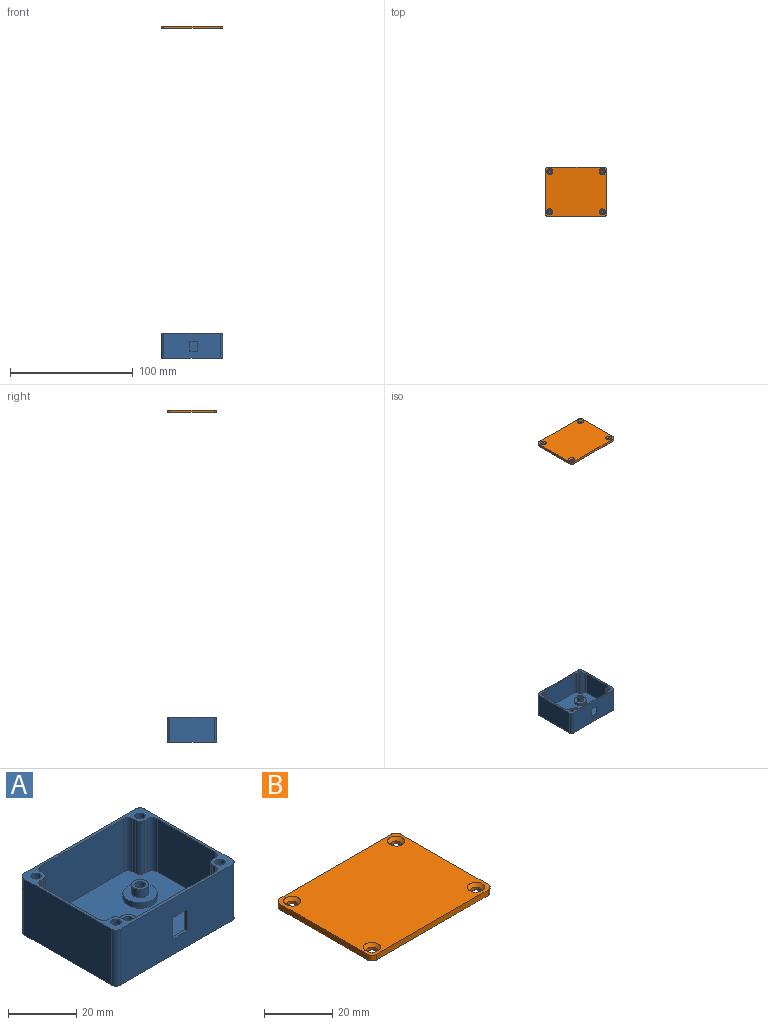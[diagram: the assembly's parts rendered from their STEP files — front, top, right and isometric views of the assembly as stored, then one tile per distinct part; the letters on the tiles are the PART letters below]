
ASSEMBLY  parts=2 mates=1
PART A: 71 faces, bbox 50x40x20 mm
  f0: plane 34x19mm, normal (0,1,0), area 598.7mm2, adj f4,f8,f51,f55,f67,f68,f69,f70
  f1: plane 46x20mm, normal (0,-1,0), area 872.7mm2, adj f8,f12,f64,f65,f67,f68,f69,f70
  f2: cylinder r=1.5mm len=4mm, axis (0,0,-1), area 37.7mm2, adj f30,f50
  f3: cylinder r=1.5mm len=4mm, axis (0,0,-1), area 37.7mm2, adj f32,f43
  f4: plane 48x38mm, normal (0,0,1), area 1563.5mm2, adj f0,f5,f6,f7,f13,f14,f15,f16
  f5: plane 24x19mm, normal (-1,0,0), area 456mm2, adj f4,f8,f53,f57
  f6: plane 34x19mm, normal (0,-1,0), area 646mm2, adj f4,f8,f58,f60
  f7: plane 24x19mm, normal (1,0,0), area 456mm2, adj f4,f8,f56,f62
  f8: plane 50x40mm, normal (0,0,1), area 247.7mm2, adj f0,f1,f5,f6,f7,f9,f10,f11
  f9: plane 46x20mm, normal (0,1,0), area 920mm2, adj f8,f12,f63,f66
  f10: plane 36x20mm, normal (-1,0,0), area 720mm2, adj f8,f12,f63,f64
  f11: plane 36x20mm, normal (1,0,0), area 720mm2, adj f8,f12,f65,f66
  f12: plane 50x40mm, normal (0,0,-1), area 1949.8mm2, adj f1,f9,f10,f11,f37,f38,f39,f40
  f13: plane 19x1mm, normal (0,-1,0), area 19mm2, adj f4,f8,f61,f62
  f14: plane 19x1mm, normal (1,0,0), area 19mm2, adj f4,f8,f60,f61
  f15: plane 19x1mm, normal (0,-1,0), area 19mm2, adj f4,f8,f57,f59
  f16: plane 19x1mm, normal (-1,0,0), area 19mm2, adj f4,f8,f58,f59
  f17: plane 19x1mm, normal (0,1,0), area 19mm2, adj f4,f8,f52,f53
  f18: plane 19x1mm, normal (-1,0,0), area 19mm2, adj f4,f8,f51,f52
  f19: plane 19x1mm, normal (0,1,0), area 19mm2, adj f4,f8,f54,f56
  f20: plane 19x1mm, normal (1,0,0), area 19mm2, adj f4,f8,f54,f55
  f21: cylinder r=1.5mm len=10mm, axis (0,0,1), area 94.2mm2, adj f8,f22
  f22: plane 3x3mm, normal (0,0,1), area 7.1mm2, adj f21
  f23: cylinder r=1.5mm len=10mm, axis (0,0,1), area 94.2mm2, adj f8,f24
  f24: plane 3x3mm, normal (0,0,1), area 7.1mm2, adj f23
  f25: cylinder r=1.5mm len=10mm, axis (0,0,1), area 94.2mm2, adj f8,f26
  f26: plane 3x3mm, normal (0,0,1), area 7.1mm2, adj f25
  f27: cylinder r=1.5mm len=10mm, axis (0,0,1), area 94.2mm2, adj f8,f28
  f28: plane 3x3mm, normal (0,0,1), area 7.1mm2, adj f27
  f29: cylinder r=2.5mm len=5mm, axis (0,0,-1), area 47.1mm2, adj f30,f34
  f30: plane 5x5mm, normal (0,0,1), area 12.6mm2, adj f2,f29
  f31: cylinder r=2.5mm len=5mm, axis (0,0,-1), area 47.1mm2, adj f32,f36
  f32: plane 5x5mm, normal (0,0,1), area 12.6mm2, adj f3,f31
  f33: cylinder r=5mm len=10mm, axis (0,0,-1), area 62.8mm2, adj f4,f34
  f34: plane 10x10mm, normal (0,0,1), area 58.9mm2, adj f29,f33
  f35: cylinder r=5mm len=10mm, axis (0,0,-1), area 62.8mm2, adj f4,f36
  f36: plane 10x10mm, normal (0,0,1), area 58.9mm2, adj f31,f35
  f37: plane 3x2mm, normal (1,-0.02,0), area 6mm2, adj f12,f38,f42,f43
  f38: plane 2.63x2mm, normal (0.48,-0.88,0), area 6mm2, adj f12,f37,f39,f43
  f39: plane 2.57x2mm, normal (-0.52,-0.86,0), area 6mm2, adj f12,f38,f40,f43
  f40: plane 3x2mm, normal (-1,0.02,0), area 6mm2, adj f12,f39,f41,f43
  f41: plane 2.63x2mm, normal (-0.48,0.88,0), area 6mm2, adj f12,f40,f42,f43
  f42: plane 2.57x2mm, normal (0.52,0.86,0), area 6mm2, adj f12,f37,f41,f43
  f43: plane 6x5.26mm, normal (0,0,-1), area 16.3mm2, adj f3,f37,f38,f39,f40,f41,f42
  f44: plane 2.97x2mm, normal (0.99,-0.14,0), area 6mm2, adj f12,f45,f49,f50
  f45: plane 2.79x2mm, normal (0.37,-0.93,0), area 6mm2, adj f12,f44,f46,f50
  f46: plane 2.36x2mm, normal (-0.62,-0.79,0), area 6mm2, adj f12,f45,f47,f50
  f47: plane 2.97x2mm, normal (-0.99,0.14,0), area 6mm2, adj f12,f46,f48,f50
  f48: plane 2.79x2mm, normal (-0.37,0.93,0), area 6mm2, adj f12,f47,f49,f50
  f49: plane 2.36x2mm, normal (0.62,0.79,0), area 6mm2, adj f12,f44,f48,f50
  f50: plane 5.94x5.57mm, normal (0,0,-1), area 16.3mm2, adj f2,f44,f45,f46,f47,f48,f49
  f51: cylinder r=2mm len=19mm, axis (0,0,-1), area 59.7mm2, adj f0,f4,f8,f18
  f52: cylinder r=2mm len=19mm, axis (0,0,1), area 59.7mm2, adj f4,f8,f17,f18
  f53: cylinder r=2mm len=19mm, axis (0,0,-1), area 59.7mm2, adj f4,f5,f8,f17
  f54: cylinder r=2mm len=19mm, axis (0,0,1), area 59.7mm2, adj f4,f8,f19,f20
  f55: cylinder r=2mm len=19mm, axis (0,0,1), area 59.7mm2, adj f0,f4,f8,f20
  f56: cylinder r=2mm len=19mm, axis (0,0,-1), area 59.7mm2, adj f4,f7,f8,f19
  f57: cylinder r=2mm len=19mm, axis (0,0,1), area 59.7mm2, adj f4,f5,f8,f15
  f58: cylinder r=2mm len=19mm, axis (0,0,-1), area 59.7mm2, adj f4,f6,f8,f16
  f59: cylinder r=2mm len=19mm, axis (0,0,1), area 59.7mm2, adj f4,f8,f15,f16
  f60: cylinder r=2mm len=19mm, axis (0,0,1), area 59.7mm2, adj f4,f6,f8,f14
  f61: cylinder r=2mm len=19mm, axis (0,0,1), area 59.7mm2, adj f4,f8,f13,f14
  f62: cylinder r=2mm len=19mm, axis (0,0,1), area 59.7mm2, adj f4,f7,f8,f13
  f63: cylinder r=2mm len=20mm, axis (0,0,1), area 62.8mm2, adj f8,f9,f10,f12
  f64: cylinder r=2mm len=20mm, axis (0,0,-1), area 62.8mm2, adj f1,f8,f10,f12
  f65: cylinder r=2mm len=20mm, axis (0,0,1), area 62.8mm2, adj f1,f8,f11,f12
  f66: cylinder r=2mm len=20mm, axis (0,0,-1), area 62.8mm2, adj f8,f9,f11,f12
  f67: plane 6.19x1mm, normal (0,0,-1), area 6.2mm2, adj f0,f1,f68,f70
  f68: plane 7.64x1mm, normal (1,0,0), area 7.6mm2, adj f0,f1,f67,f69
  f69: plane 6.19x1mm, normal (0,0,1), area 6.2mm2, adj f0,f1,f68,f70
  f70: plane 7.64x1mm, normal (-1,0,0), area 7.6mm2, adj f0,f1,f67,f69
PART B: 18 faces, bbox 50x40x2 mm
  f0: plane 36x2mm, normal (-1,0,0), area 72mm2, adj f4,f5,f14,f17
  f1: plane 46x2mm, normal (0,-1,0), area 92mm2, adj f4,f5,f14,f15
  f2: plane 36x2mm, normal (1,0,0), area 72mm2, adj f4,f5,f15,f16
  f3: plane 46x2mm, normal (0,1,0), area 92mm2, adj f4,f5,f16,f17
  f4: plane 50x40mm, normal (0,0,1), area 1918mm2, adj f0,f1,f2,f3,f10,f11,f12,f13
  f5: plane 50x40mm, normal (0,0,-1), area 1968.3mm2, adj f0,f1,f2,f3,f6,f7,f8,f9
  f6: cylinder r=1.5mm len=3mm, axis (0,0,1), area 9.4mm2, adj f5,f11
  f7: cylinder r=1.5mm len=3mm, axis (0,0,1), area 9.4mm2, adj f5,f13
  f8: cylinder r=1.5mm len=3mm, axis (0,0,1), area 9.4mm2, adj f5,f12
  f9: cylinder r=1.5mm len=3mm, axis (0,0,1), area 9.4mm2, adj f5,f10
  f10: cone r=1.5mm half-angle=45deg, axis (0,0,1), area 17.8mm2, adj f4,f9
  f11: cone r=1.5mm half-angle=45deg, axis (0,0,1), area 17.8mm2, adj f4,f6
  f12: cone r=1.5mm half-angle=45deg, axis (0,0,1), area 17.8mm2, adj f4,f8
  f13: cone r=1.5mm half-angle=45deg, axis (0,0,1), area 17.8mm2, adj f4,f7
  f14: cylinder r=2mm len=2mm, axis (0,0,1), area 6.3mm2, adj f0,f1,f4,f5
  f15: cylinder r=2mm len=2mm, axis (0,0,-1), area 6.3mm2, adj f1,f2,f4,f5
  f16: cylinder r=2mm len=2mm, axis (0,0,1), area 6.3mm2, adj f2,f3,f4,f5
  f17: cylinder r=2mm len=2mm, axis (0,0,-1), area 6.3mm2, adj f0,f3,f4,f5
PLACE A t=(-20.94,-10.23,20.1)mm fixed
PLACE B t=(-86.97,-9.1,289.06)mm
MATE slider A.f23 <-> B.f9  axis (0,0,1) through (-29.98,7.1,40.1)mm
